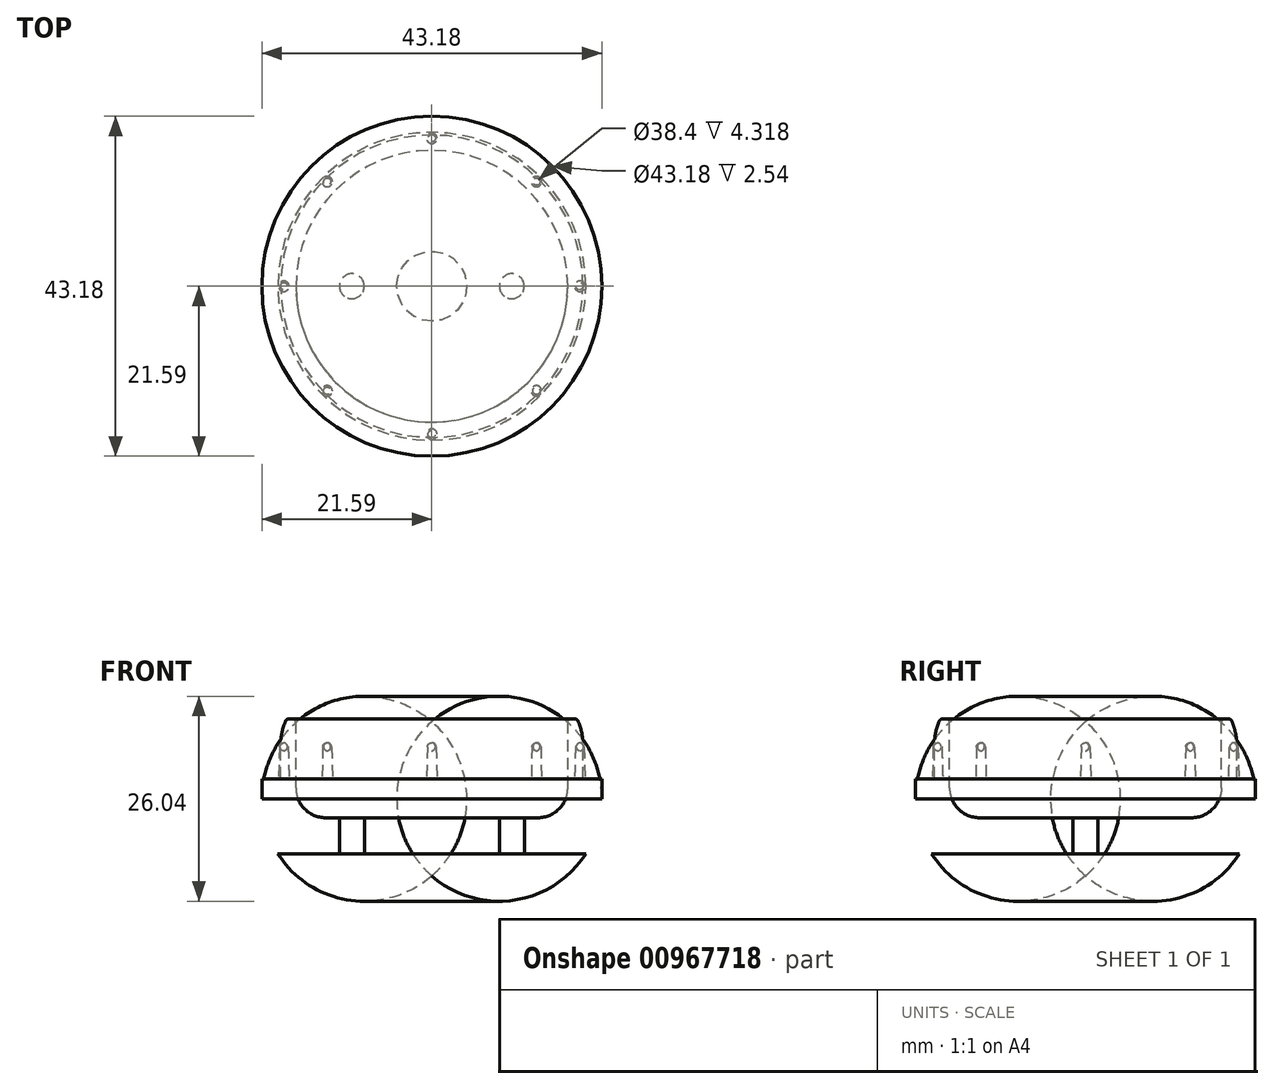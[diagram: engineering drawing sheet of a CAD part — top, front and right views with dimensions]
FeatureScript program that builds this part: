
annotation { "Feature Type Name" : "Feature", "Feature Type Description" : "" }
export const myFeature = defineFeature(function(context is Context, id is Id, definition is map)
    precondition{}
    {
        {
            var Q0;
            Q0=qCreatedBy(makeId("Front.planeOp"),FACE);
            var sketch = newSketch(context, id + "F0", { "sketchPlane" : qUnion([Q0])});
            skLineSegment(sketch, "E0", {"start": v(17.27, 0) * mm, "end": v(17.27, -8.76) * mm});
            skLineSegment(sketch, "E1", {"start": v(13.46, -12.57) * mm, "end": v(0, -12.57) * mm});
            skLineSegment(sketch, "E2", {"start": v(0, -12.57) * mm, "end": v(0, -17.15) * mm});
            skLineSegment(sketch, "E3", {"start": v(0, -17.15) * mm, "end": v(19.56, -17.14) * mm});
            skPoint(sketch, "E4.visualSharp", {"position": v(17.27, -12.57) * mm});
            skArc(sketch, "E4.filletArc", {"start": v(13.46, -12.57) * mm, "mid": v(16.16, -11.46) * mm, "end": v(17.27, -8.76) * mm});
            skArc(sketch, "E5", {"start": v(19.56, -17.14) * mm, "mid": v(21.07, -13.8) * mm, "end": v(21.59, -10.16) * mm});
            skLineSegment(sketch, "E6", {"start": v(21.59, -7.62) * mm, "end": v(19.2, -7.62) * mm});
            skLineSegment(sketch, "E7", {"start": v(19.2, -7.62) * mm, "end": v(19.2, -3.3) * mm});
            skArc(sketch, "E8", {"start": v(19.2, -3.3) * mm, "mid": v(19, -1.6) * mm, "end": v(18.44, 0) * mm});
            skLineSegment(sketch, "E9", {"start": v(18.44, 0) * mm, "end": v(17.27, 0) * mm});
            skLineSegment(sketch, "E10", {"start": v(21.59, -7.62) * mm, "end": v(21.59, -10.16) * mm});
            skSolve(sketch);
        }
        {
            var Q0;
            Q0=makeQuery(id+"F0.imprint","IMPRINT",FACE,{"disambiguationData":[TD([[makeQuery(id+"F0.imprint","IMPRINT",EDGE,{"derivedFrom":sQuery(id+"F0.wireOp",EDGE,"E0")}),1.0]])]});
            var Q1;
            Q1=sQuery(id+"F0.wireOp",EDGE,"E2");
            revolve(context, id + "F1", {"surfaceOperationType" : NewSurfaceOperationType.NEW, "entities" : qUnion([Q0]), "axis" : qUnion([Q1]), "revolveType" : RevolveType.FULL});
        }
        {
            var Q0;
            Q0=makeQuery(id+"F1.opRevolve","SWEPT_FACE",FACE,{"disambiguationData":[OSD([sQuery(id+"F0.wireOp",EDGE,"E9")])]});
            var sketch = newSketch(context, id + "F2", { "sketchPlane" : qUnion([Q0])});
            skCircle(sketch, "E11", {"center": v(-10.16, 0) * mm, "radius": 1.59 * mm});
            skCircle(sketch, "E12", {"center": v(10.16, 0) * mm, "radius": 1.59 * mm});
            skSolve(sketch);
        }
        {
            var Q0;
            Q0 = qSketchRegion(id + "F2", true);
            extrude(context, id + "F3", {"entities" : qUnion([Q0]), "operationType" : NewBodyOperationType.REMOVE, "oppositeDirection" : true, "depth" : 25.4 * mm, "offsetDistance" : 25.4 * mm});
        }
        {
            var Q0;
            Q0=makeQuery(id+"F1.opRevolve","SWEPT_EDGE",EDGE,{"disambiguationData":[OSD([sQuery(id+"F0.wireOp",EDGE,"E8"),sQuery(id+"F0.wireOp",EDGE,"E9")])]});
            var Q1;
            Q1=makeQuery(id+"F1.opRevolve","SWEPT_EDGE",EDGE,{"disambiguationData":[OSD([sQuery(id+"F0.wireOp",EDGE,"E0"),sQuery(id+"F0.wireOp",EDGE,"E9")])]});
            fillet(context, id + "F4", {"entities" : qUnion([Q0, Q1]), "radius" : 0.5 * mm, "tangentPropagation" : true, "allowEdgeOverflow" : false});
        }
        {
            var Q0;
            Q0=qCreatedBy(makeId("Front.planeOp"),FACE);
            var sketch = newSketch(context, id + "F5", { "sketchPlane" : qUnion([Q0])});
            skLineSegment(sketch, "E13", {"start": v(18.8, -7.62) * mm, "end": v(19.46, -7.62) * mm});
            skLineSegment(sketch, "E14", {"start": v(19.46, -7.62) * mm, "end": v(19.35, -3.56) * mm});
            skLineSegment(sketch, "E15", {"start": v(18.8, -7.62) * mm, "end": v(18.8, -3.06) * mm});
            skArc(sketch, "E16", {"start": v(19.35, -3.56) * mm, "mid": v(19.18, -3.19) * mm, "end": v(18.8, -3.06) * mm});
            skSolve(sketch);
        }
        {
            var Q0;
            Q0=makeQuery(id+"F5.imprint","IMPRINT",FACE,{"disambiguationData":[TD([[makeQuery(id+"F5.imprint","IMPRINT",EDGE,{"derivedFrom":sQuery(id+"F5.wireOp",EDGE,"E13")}),1.0]])]});
            var Q1;
            Q1=sQuery(id+"F5.wireOp",EDGE,"E15");
            revolve(context, id + "F6", {"surfaceOperationType" : NewSurfaceOperationType.NEW, "entities" : qUnion([Q0]), "axis" : qUnion([Q1]), "revolveType" : RevolveType.FULL});
        }
        {
            var Q0;
            Q0=makeQuery(id+"F6.opRevolve","SWEPT_BODY",BODY,{"disambiguationData":[OSD([sQuery(id+"F5.wireOp",EDGE,"E13"),sQuery(id+"F5.wireOp",EDGE,"E14"),sQuery(id+"F5.wireOp",EDGE,"E15"),sQuery(id+"F5.wireOp",EDGE,"E16")])]});
            var Q1;
            Q1=makeQuery(id+"F1.opRevolve","SWEPT_EDGE",EDGE,{"disambiguationData":[OSD([sQuery(id+"F0.wireOp",EDGE,"E5"),sQuery(id+"F0.wireOp",EDGE,"E10")])]});
            circularPattern(context, id + "F7", {"entities" : qUnion([Q0]), "axis" : qUnion([Q1]), "angle" : 360 * degree, "instanceCount" : 8, "equalSpace" : true});
        }
    });
